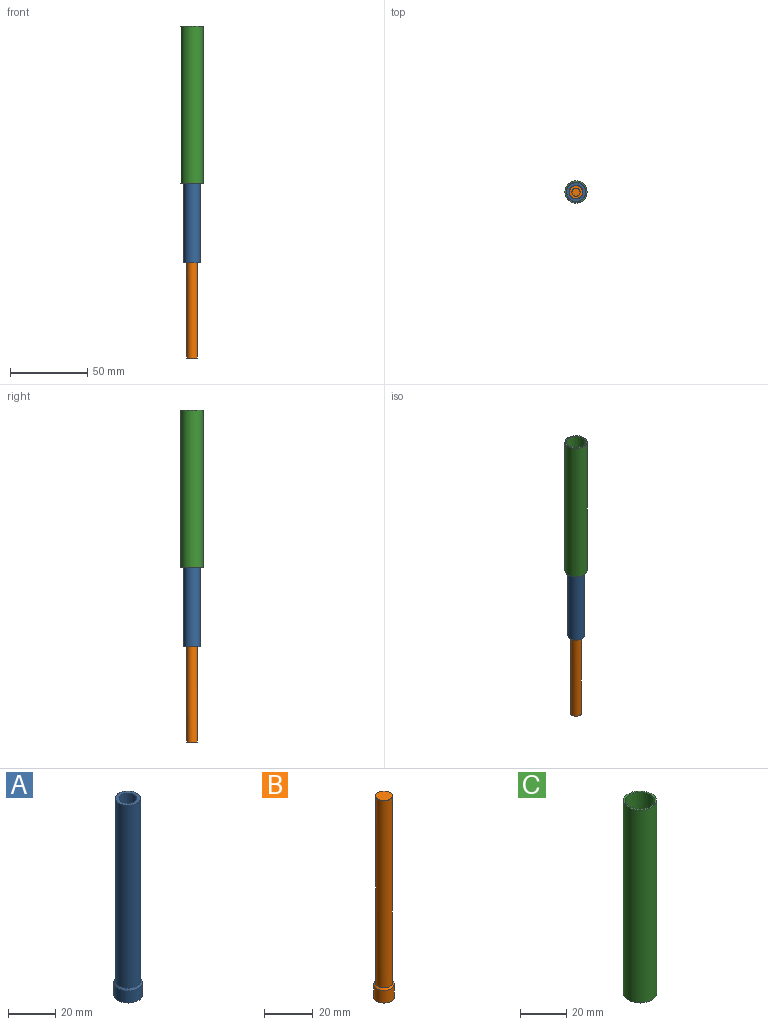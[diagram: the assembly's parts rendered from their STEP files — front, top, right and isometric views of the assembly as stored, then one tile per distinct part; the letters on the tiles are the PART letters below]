
ASSEMBLY  parts=3 mates=3
PART A: 8 faces, bbox 12.1x12.1x101.6 mm
  f0: cylinder r=4.51mm len=94.46mm, axis (0,0,-1), area 2679.5mm2, adj f3,f7
  f1: cylinder r=5.31mm len=94.49mm, axis (0,0,-1), area 3151.6mm2, adj f2,f5
  f2: plane 10.62x10.62mm, normal (0,0,1), area 45mm2, adj f1,f6
  f3: plane 12.14x12.14mm, normal (0,0,-1), area 51.7mm2, adj f0,f4
  f4: cylinder r=6.07mm len=12.14mm, axis (0,0,-1), area 242.2mm2, adj f3,f5
  f5: cone r=5.31mm half-angle=45deg, axis (0,0,-1), area 38.5mm2, adj f1,f4
  f6: cylinder r=3.72mm len=7.44mm, axis (0,0,1), area 148.5mm2, adj f2,f7
  f7: cone r=4.51mm half-angle=45deg, axis (0,0,-1), area 29mm2, adj f0,f6
PART B: 7 faces, bbox 8.5x8.5x101.6 mm
  f0: cylinder r=2.67mm len=98.43mm, axis (0,0,-1), area 1653.3mm2, adj f3,f5
  f1: cylinder r=3.47mm len=94.46mm, axis (0,0,-1), area 2057.7mm2, adj f2,f6
  f2: plane 6.93x6.93mm, normal (0,0,1), area 37.8mm2, adj f1
  f3: plane 8.46x8.46mm, normal (0,0,-1), area 33.7mm2, adj f0,f4
  f4: cylinder r=4.23mm len=8.46mm, axis (0,0,-1), area 169.6mm2, adj f3,f6
  f5: plane 5.35x5.35mm, normal (0,0,-1), area 22.5mm2, adj f0
  f6: cone r=3.47mm half-angle=45deg, axis (0,0,-1), area 26.1mm2, adj f1,f4
PART C: 6 faces, bbox 14.3x14.3x101.6 mm
  f0: cylinder r=6.35mm len=94.46mm, axis (0,0,-1), area 3768.6mm2, adj f2,f5
  f1: cylinder r=7.14mm len=101.6mm, axis (0,0,-1), area 4560.4mm2, adj f2,f3
  f2: plane 14.29x14.29mm, normal (0,0,1), area 33.6mm2, adj f0,f1
  f3: plane 14.29x14.29mm, normal (0,0,-1), area 63.3mm2, adj f1,f4
  f4: cylinder r=5.56mm len=11.11mm, axis (0,0,-1), area 221.7mm2, adj f3,f5
  f5: cone r=6.35mm half-angle=45deg, axis (0,0,1), area 42mm2, adj f0,f4
PLACE A rot(axis=(0.74,-0.67,0),180deg) t=(-4.04,-22.84,39.14)mm
PLACE B rot(axis=(0.91,0.41,0),180deg) t=(-4.04,-22.84,-22.43)mm
PLACE C t=(-4.04,-22.84,-11.09)mm fixed
MATE cylindrical A.f1 <-> C.f1  axis (0,0,1) through (-4.04,-22.84,-15.22)mm
MATE cylindrical A.f1 <-> A.f1  axis (0,0,1) through (-4.04,-22.84,-15.22)mm
MATE cylindrical A.f1 <-> B.f1  axis (0,0,1) through (-4.04,-22.84,-62.46)mm
